# Revit family: 540_Sliding_Window_XXXX_Custom
name_source: partatom
category: Windows
revit_build: Autodesk Revit 2014 (Build: 20130308_1515(x64)
units: mm (PartAtom-declared; Revit-internal decimal feet)

## types (1)
- 540SW-XXXX-Custom
    Astragal Sash Gap = 1 mm  [stored 0.00328084 ft]
    Custom SHGC Value = 0
    Default Sill Height = 800 mm
    Description = Sliding window, XXXX custom
    Frame Thickness = 54 mm  [stored 0.177165 ft]
    Heavy Duty Handle Gap = 27 mm
    Limit Sash Height Max = 1500 mm  [stored 4.92126 ft]
    Limit Sash Height Min = 300 mm  [stored 0.984252 ft]
    Limit Sash Width Max = 1200 mm  [stored 3.93701 ft]
    Limit Sash Width Min = 300 mm  [stored 0.984252 ft]
    Limit Window Height Max = 1580 mm
    Limit Window Height Min = 380 mm
    Limit Window Width Max = 4760 mm
    Limit Window Width Min = 1160 mm
    Manufacturer = Crealco
    Model = 540
    Sash Frame Seal = 3 mm  [stored 0.00984252 ft]
    URL = http://www.crealco.co.za
    Wall Closure = By host

note: [stored X ft] marks values corroborated as IEEE doubles in the binary element streams (Revit-internal decimal feet)

## geometry (parser evidence)
native form markers: Sweep x8
no freeform markers — native parametric forms only
